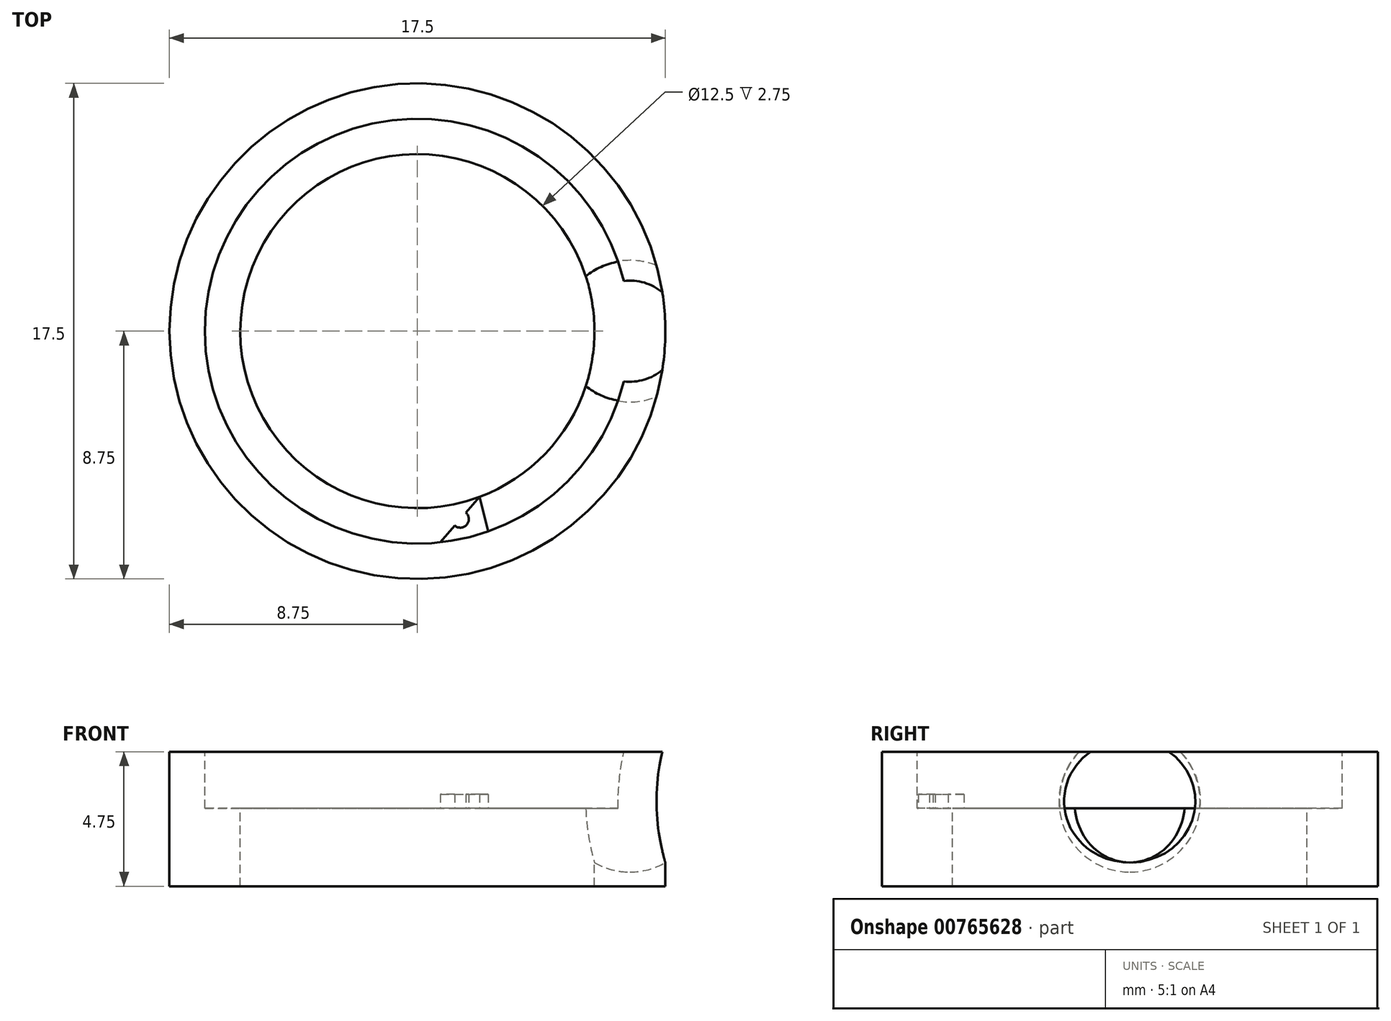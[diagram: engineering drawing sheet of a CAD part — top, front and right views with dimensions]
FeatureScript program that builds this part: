
annotation { "Feature Type Name" : "Feature", "Feature Type Description" : "" }
export const myFeature = defineFeature(function(context is Context, id is Id, definition is map)
    precondition{}
    {
        {
            var Q0;
            Q0=qCreatedBy(makeId("Front.planeOp"),FACE);
            var sketch = newSketch(context, id + "F0", { "sketchPlane" : qUnion([Q0])});
            skLineSegment(sketch, "E0", {"start": v(0, 9.66) * mm, "end": v(0, -12.64) * mm});
            skLineSegment(sketch, "E1", {"start": v(6.25, 0) * mm, "end": v(8.75, 0) * mm});
            skLineSegment(sketch, "E2", {"start": v(6.25, -3.5) * mm, "end": v(8.75, -3.5) * mm});
            skLineSegment(sketch, "E3", {"start": v(8.75, 3.5) * mm, "end": v(6.25, 3.5) * mm});
            skLineSegment(sketch, "E4.0", {"start": v(6.25, 0) * mm, "end": v(6.25, -3.5) * mm});
            skLineSegment(sketch, "E4.1", {"start": v(6.25, 3.5) * mm, "end": v(6.25, 0) * mm});
            skPoint(sketch, "E5.orphan", {"position": v(9, -3.5) * mm});
            skPoint(sketch, "E6.orphan", {"position": v(6, 0) * mm});
            skPoint(sketch, "E7.orphan", {"position": v(6, 3.5) * mm});
            skLineSegment(sketch, "E8.0", {"start": v(8.75, -3.5) * mm, "end": v(8.75, 3.5) * mm});
            skPoint(sketch, "E9.orphan", {"position": v(9, 0) * mm});
            skSolve(sketch);
        }
        {
            var Q0;
            Q0=qSketchRegion(id+"F0",true);
            var Q1;
            Q1=sQuery(id+"F0.wireOp",EDGE,"E0");
            revolve(context, id + "F1", {"surfaceOperationType" : NewSurfaceOperationType.NEW, "entities" : qUnion([Q0]), "axis" : qUnion([Q1]), "revolveType" : RevolveType.FULL});
        }
        {
            var Q0;
            Q0=qCreatedBy(makeId("Front.planeOp"),FACE);
            var sketch = newSketch(context, id + "F2", { "sketchPlane" : qUnion([Q0])});
            skLineSegment(sketch, "E10", {"start": v(0, 0) * mm, "end": v(6.25, 0) * mm});
            skLineSegment(sketch, "E11", {"start": v(6.25, 0) * mm, "end": v(6.25, 0) * mm});
            skLineSegment(sketch, "E12", {"start": v(6.25, 0) * mm, "end": v(8.75, 0) * mm});
            skCircle(sketch, "E13", {"center": v(7.5, 0) * mm, "radius": 2.5 * mm});
            skLineSegment(sketch, "E14", {"start": v(7.5, 2.5) * mm, "end": v(7.5, -2.5) * mm});
            skSolve(sketch);
        }
        {
            var Q0;
            {var subQ0=sQuery(id+"F2.wireOp",EDGE,"E14");var subQ1=sQuery(id+"F2.wireOp",EDGE,"E13");var subQ2=makeQuery(id+"F2.imprint","INTERSECT",VERTEX,{"disambiguationData":[OD(0.0)],"derivedFrom":[subQ1,subQ0]});Q0=makeQuery(id+"F2.imprint","IMPRINT",FACE,{"disambiguationData":[TD([[makeQuery(id+"F2.imprint","IMPRINT",EDGE,{"disambiguationData":[TD([[subQ2,1.0]])],"derivedFrom":subQ1}),1.0]])]});}
            var Q1;
            Q1=sQuery(id+"F2.wireOp",EDGE,"E14");
            revolve(context, id + "F3", {"operationType" : NewBodyOperationType.REMOVE, "surfaceOperationType" : NewSurfaceOperationType.NEW, "entities" : qUnion([Q0]), "axis" : qUnion([Q1]), "revolveType" : RevolveType.FULL, "oppositeDirection" : true});
        }
        {
            var Q0;
            Q0=qCreatedBy(makeId("Front.planeOp"),FACE);
            var sketch = newSketch(context, id + "F4", { "sketchPlane" : qUnion([Q0])});
            skLineSegment(sketch, "E15", {"start": v(0, 8.37) * mm, "end": v(0, -14.66) * mm});
            skSolve(sketch);
        }
        {
            var Q0;
            Q0=qCreatedBy(makeId("Front.planeOp"),FACE);
            var sketch = newSketch(context, id + "F5", { "sketchPlane" : qUnion([Q0])});
            skLineSegment(sketch, "E16", {"start": v(0, 0) * mm, "end": v(0, 1.75) * mm});
            skLineSegment(sketch, "E17", {"start": v(0, 1.75) * mm, "end": v(-9, 1.75) * mm});
            skLineSegment(sketch, "E18.bottom", {"start": v(-9, 1.75) * mm, "end": v(9.16, 1.75) * mm});
            skLineSegment(sketch, "E18.top", {"start": v(-9, 4.49) * mm, "end": v(9.16, 4.49) * mm});
            skLineSegment(sketch, "E18.left", {"start": v(-9, 1.75) * mm, "end": v(-9, 4.49) * mm});
            skLineSegment(sketch, "E18.right", {"start": v(9.16, 1.75) * mm, "end": v(9.16, 4.49) * mm});
            skLineSegment(sketch, "E19", {"start": v(0, 0) * mm, "end": v(0, -3) * mm});
            skLineSegment(sketch, "E20.bottom", {"start": v(-9.2, -3) * mm, "end": v(9.16, -3) * mm});
            skLineSegment(sketch, "E20.top", {"start": v(-9.2, -4.73) * mm, "end": v(9.16, -4.73) * mm});
            skLineSegment(sketch, "E20.left", {"start": v(-9.2, -3) * mm, "end": v(-9.2, -4.73) * mm});
            skLineSegment(sketch, "E20.right", {"start": v(9.16, -3) * mm, "end": v(9.16, -4.73) * mm});
            skSolve(sketch);
        }
        {
            var Q0;
            Q0=qSketchRegion(id+"F5",true);
            extrude(context, id + "F6", {"entities" : qUnion([Q0]), "operationType" : NewBodyOperationType.REMOVE, "endBound" : BoundingType.SYMMETRIC, "oppositeDirection" : true, "depth" : 25 * mm, "offsetDistance" : 25 * mm});
        }
        {
            var Q0;
            {var subQ0=sQuery(id+"F2.wireOp",EDGE,"E13");Q0=makeQuery(id+"F6.boolean.opBoolean","COPY",FACE,{"disambiguationData":[TD([makeQuery(id+"F1.opRevolve","SWEPT_FACE",FACE,{"disambiguationData":[OSD([sQuery(id+"F0.wireOp",EDGE,"E4.0"),sQuery(id+"F0.wireOp",EDGE,"E4.1")])]}),makeQuery(id+"F1.opRevolve","SWEPT_FACE",FACE,{"disambiguationData":[OSD([sQuery(id+"F0.wireOp",EDGE,"E8.0")])]}),makeQuery(id+"F6Gl4txAeZpl2Zy_1.1.F3.boolean.opBoolean","COPY",FACE,{"derivedFrom":makeQuery(id+"F6Gl4txAeZpl2Zy_1.1.F3.opRevolve","SWEPT_FACE",FACE,{"disambiguationData":[OSD([subQ0])]})}),makeQuery(id+"F6Gl4txAeZpl2Zy_1.2.F3.boolean.opBoolean","COPY",FACE,{"derivedFrom":makeQuery(id+"F6Gl4txAeZpl2Zy_1.2.F3.opRevolve","SWEPT_FACE",FACE,{"disambiguationData":[OSD([subQ0])]})})])],"derivedFrom":makeQuery(id+"F6.opExtrude","SWEPT_FACE",FACE,{"disambiguationData":[OSD([sQuery(id+"F5.wireOp",EDGE,"E18.bottom")])]})});}
            var sketch = newSketch(context, id + "F7", { "sketchPlane" : qUnion([Q0])});
            skCircle(sketch, "E21", {"center": v(0, 0) * mm, "radius": 7.5 * mm});
            skSolve(sketch);
        }
        {
            var Q0;
            Q0=qSketchRegion(id+"F7",true);
            extrude(context, id + "F8", {"entities" : qUnion([Q0]), "operationType" : NewBodyOperationType.REMOVE, "oppositeDirection" : true, "depth" : 2 * mm, "offsetDistance" : 25 * mm});
        }
        {
            var Q0;
            {var subQ0=sQuery(id+"F2.wireOp",EDGE,"E13");var subQ1=sQuery(id+"F7.wireOp",EDGE,"E21");Q0=makeQuery(id+"F8.boolean.opBoolean","COPY",FACE,{"disambiguationData":[TD([makeQuery(id+"F1.opRevolve","SWEPT_FACE",FACE,{"disambiguationData":[OSD([sQuery(id+"F0.wireOp",EDGE,"E4.0"),sQuery(id+"F0.wireOp",EDGE,"E4.1")])]}),makeQuery(id+"F6Gl4txAeZpl2Zy_1.1.F3.boolean.opBoolean","COPY",FACE,{"derivedFrom":makeQuery(id+"F6Gl4txAeZpl2Zy_1.1.F3.opRevolve","SWEPT_FACE",FACE,{"disambiguationData":[OSD([subQ0])]})}),makeQuery(id+"F6Gl4txAeZpl2Zy_1.2.F3.boolean.opBoolean","COPY",FACE,{"derivedFrom":makeQuery(id+"F6Gl4txAeZpl2Zy_1.2.F3.opRevolve","SWEPT_FACE",FACE,{"disambiguationData":[OSD([subQ0])]})}),makeQuery(id+"F8.opExtrude","SWEPT_FACE",FACE,{"disambiguationData":[OSD([subQ1])]})])],"derivedFrom":makeQuery(id+"F8.opExtrude","CAP_FACE",FACE,{"disambiguationData":[OSD([subQ1])],"isStart":false})});}
            var sketch = newSketch(context, id + "F9", { "sketchPlane" : qUnion([Q0])});
            skLineSegment(sketch, "E22", {"start": v(0.57, -6.22) * mm, "end": v(2.5, -7.07) * mm});
            skLineSegment(sketch, "E23", {"start": v(2.5, -7.07) * mm, "end": v(2.19, -5.85) * mm});
            skLineSegment(sketch, "E24", {"start": v(2.19, -5.85) * mm, "end": v(0.81, -7.46) * mm});
            skLineSegment(sketch, "E25", {"start": v(0.81, -7.46) * mm, "end": v(0.57, -6.22) * mm});
            skCircle(sketch, "E26", {"center": v(1.52, -6.64) * mm, "radius": 0.4 * mm});
            skCircle(sketch, "E27", {"center": v(1.52, -6.64) * mm, "radius": 0.3 * mm});
            skSolve(sketch);
        }
        {
            var Q0;
            {var subQ0=sQuery(id+"F9.wireOp",EDGE,"E26");var subQ1=sQuery(id+"F9.wireOp",EDGE,"E22");var subQ2=makeQuery(id+"F9.imprint","INTERSECT",VERTEX,{"disambiguationData":[OD(0.0)],"derivedFrom":[subQ1,subQ0]});Q0=makeQuery(id+"F9.imprint","IMPRINT",FACE,{"disambiguationData":[TD([[makeQuery(id+"F9.imprint","IMPRINT",EDGE,{"disambiguationData":[TD([[subQ2,-1.0]])],"derivedFrom":subQ1}),1.0]])]});}
            var Q1;
            {var subQ0=sQuery(id+"F9.wireOp",EDGE,"E27");var subQ1=sQuery(id+"F9.wireOp",EDGE,"E22");var subQ2=makeQuery(id+"F9.imprint","INTERSECT",VERTEX,{"disambiguationData":[OD(1.0)],"derivedFrom":[subQ1,subQ0]});Q1=makeQuery(id+"F9.imprint","IMPRINT",FACE,{"disambiguationData":[TD([[makeQuery(id+"F9.imprint","IMPRINT",EDGE,{"disambiguationData":[TD([[subQ2,-1.0]])],"derivedFrom":subQ1}),1.0]])]});}
            var Q2;
            {var subQ0=sQuery(id+"F9.wireOp",EDGE,"E27");var subQ1=sQuery(id+"F9.wireOp",EDGE,"E22");var subQ2=makeQuery(id+"F9.imprint","INTERSECT",VERTEX,{"disambiguationData":[OD(1.0)],"derivedFrom":[subQ1,subQ0]});Q2=makeQuery(id+"F9.imprint","IMPRINT",FACE,{"disambiguationData":[TD([[makeQuery(id+"F9.imprint","IMPRINT",EDGE,{"disambiguationData":[TD([[subQ2,-1.0]])],"derivedFrom":subQ1}),-1.0]])]});}
            var Q3;
            {var subQ0=sQuery(id+"F9.wireOp",EDGE,"E26");var subQ1=sQuery(id+"F9.wireOp",EDGE,"E22");var subQ2=makeQuery(id+"F9.imprint","INTERSECT",VERTEX,{"disambiguationData":[OD(0.0)],"derivedFrom":[subQ1,subQ0]});Q3=makeQuery(id+"F9.imprint","IMPRINT",FACE,{"disambiguationData":[TD([[makeQuery(id+"F9.imprint","IMPRINT",EDGE,{"disambiguationData":[TD([[subQ2,-1.0]])],"derivedFrom":subQ1}),-1.0]])]});}
            extrude(context, id + "F10", {"entities" : qUnion([Q0, Q1, Q2, Q3]), "operationType" : NewBodyOperationType.ADD, "depth" : 0.5 * mm, "offsetDistance" : 25 * mm});
        }
        {
            var Q0;
            Q0=qCreatedBy(makeId("Front.planeOp"),FACE);
            var sketch = newSketch(context, id + "F11", { "sketchPlane" : qUnion([Q0])});
            skLineSegment(sketch, "E28", {"start": v(0, 4.8) * mm, "end": v(0, -5.9) * mm});
            skSolve(sketch);
        }
    });
